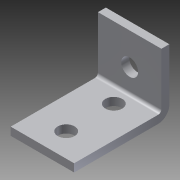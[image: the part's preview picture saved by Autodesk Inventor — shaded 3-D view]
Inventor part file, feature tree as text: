
AUTODESK INVENTOR PART (.ipt)
format: ipt  version: 2013 (Build 170138000, 138)  size: 118,784 bytes
history: native  units: in
note: dims shown in document units (in); Inventor stores cm internally (conversion verified against a paired STEP export)
features: sheet_metal_op x4, sketch x3, other x3
ambient origin geometry x8: Origin, YZ Plane, XZ Plane, XY Plane, X Axis, Y Axis, Z Axis, Center Point
bodies: Solid1 (feature_tree)
feature tree (10):
  sheet_metal_op  "Face1"
  sheet_metal_op  "Flange1"
  sketch  "Sketch1"  dims[d0=1.0in]
  other  "Plate1"
  sketch  "Sketch2"  dims[d1=1.5in]
  other  "Plate2"
  sheet_metal_op  "Bend1"
  sheet_metal_op  "Corner1"
  sketch  "Sketch3"  dims[d2=0.266in d3=0.266in d4=0.375in d5=0.375in d6=0.5in d7=0.5in d8=0.125in d9=0.125in d10=0.0625in d11=0.25in d12=0.125in d13=1.0in d14=90.0deg d15=0.05in d16=0.5in d17=0.125in d18=0.125in d19=0.266in d20=0.5in d21=0.5in d22=0.125in d23=0.0in]
  other  "Cut1"
